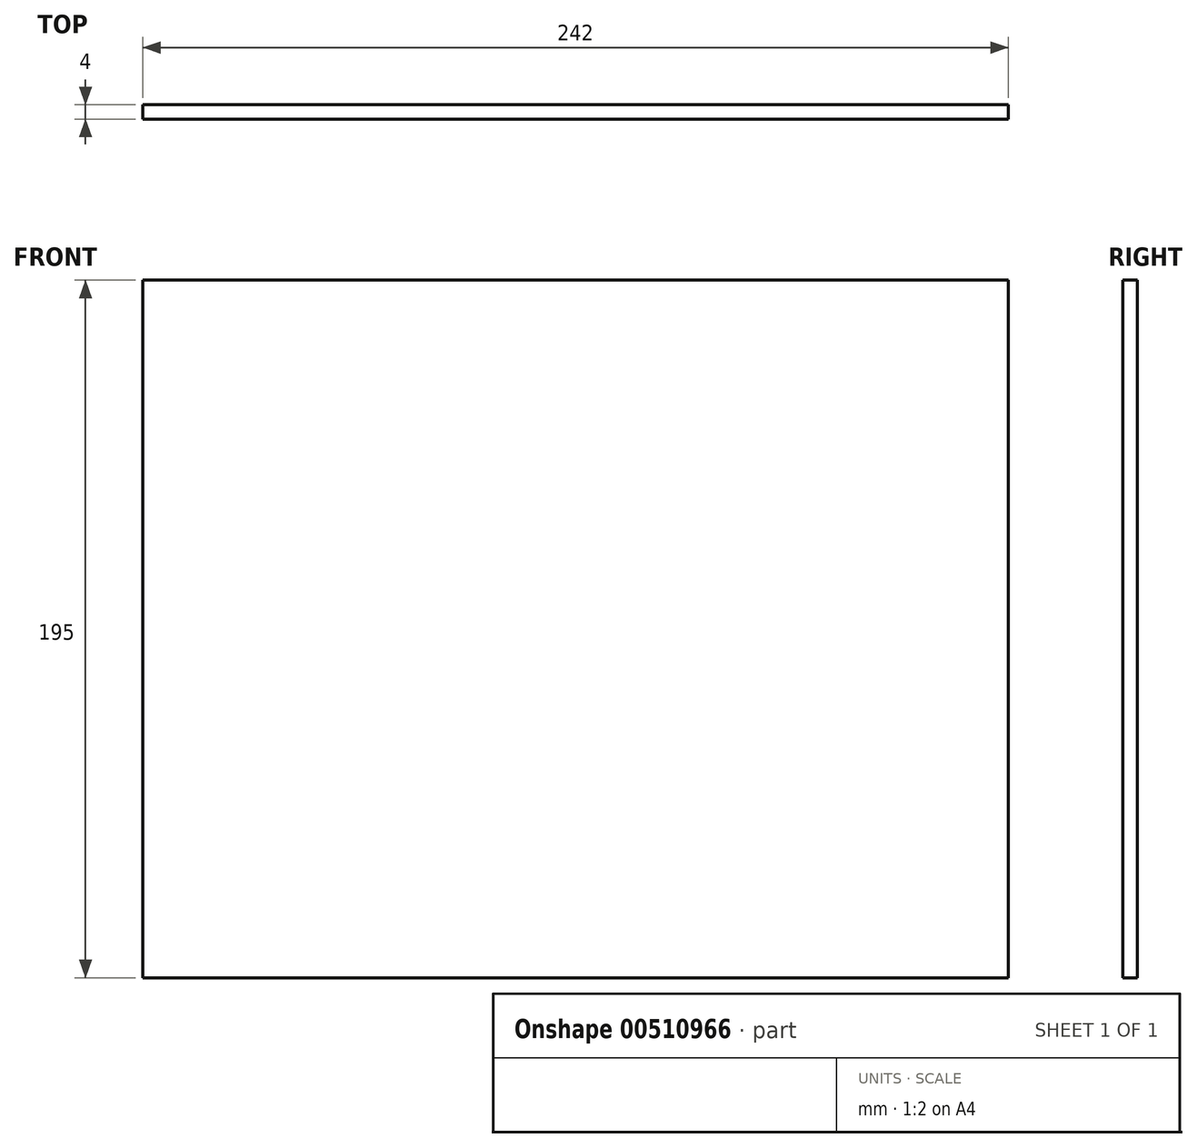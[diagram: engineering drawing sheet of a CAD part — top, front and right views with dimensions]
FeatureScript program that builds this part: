
annotation { "Feature Type Name" : "Feature", "Feature Type Description" : "" }
export const myFeature = defineFeature(function(context is Context, id is Id, definition is map)
    precondition{}
    {
        {
            var Q0;
            Q0=qCreatedBy(makeId("Front.planeOp"),FACE);
            var sketch = newSketch(context, id + "F0", { "sketchPlane" : qUnion([Q0])});
            skLineSegment(sketch, "E0.bottom", {"start": v(121, -97.5) * mm, "end": v(-121, -97.5) * mm});
            skLineSegment(sketch, "E0.top", {"start": v(121, 97.5) * mm, "end": v(-121, 97.5) * mm});
            skLineSegment(sketch, "E0.left", {"start": v(121, -97.5) * mm, "end": v(121, 97.5) * mm});
            skLineSegment(sketch, "E0.right", {"start": v(-121, -97.5) * mm, "end": v(-121, 97.5) * mm});
            skPoint(sketch, "E0.middle", {"position": v(0, 0) * mm});
            skSolve(sketch);
        }
        {
            var Q0;
            Q0=makeQuery(id+"F0.imprint","IMPRINT",FACE,{"disambiguationData":[TD([[makeQuery(id+"F0.imprint","IMPRINT",EDGE,{"derivedFrom":sQuery(id+"F0.wireOp",EDGE,"E0.bottom")}),-1.0]])]});
            extrude(context, id + "F1", {"entities" : qUnion([Q0]), "depth" : 4 * mm});
        }
    });
